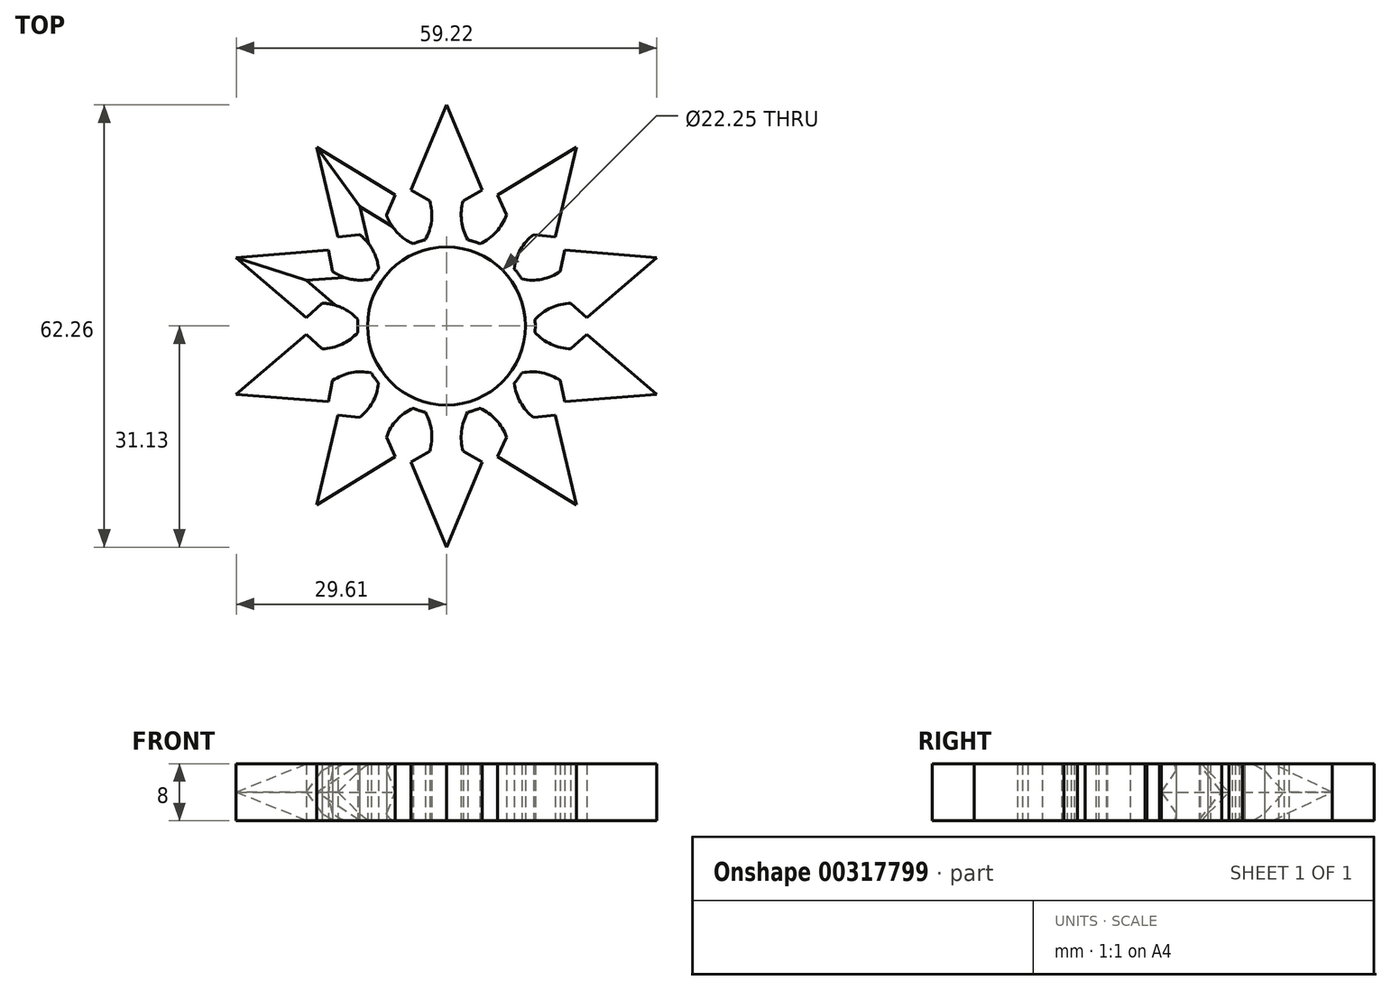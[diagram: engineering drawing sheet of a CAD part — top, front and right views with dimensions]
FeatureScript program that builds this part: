
annotation { "Feature Type Name" : "Feature", "Feature Type Description" : "" }
export const myFeature = defineFeature(function(context is Context, id is Id, definition is map)
    precondition{}
    {
        {
            var Q0;
            Q0=qCreatedBy(makeId("Top.planeOp"),FACE);
            var sketch = newSketch(context, id + "F0", { "sketchPlane" : qUnion([Q0])});
            skCircle(sketch, "E0", {"center": v(0, 0) * mm, "radius": 12.5 * mm});
            skLineSegment(sketch, "E1", {"start": v(0, 0) * mm, "end": v(0, 12.5) * mm, "construction": true});
            skPoint(sketch, "E2", {"position": v(3, 12.13) * mm});
            skPoint(sketch, "E3", {"position": v(-3, 12.13) * mm});
            skLineSegment(sketch, "E4", {"start": v(-3, 12.13) * mm, "end": v(-3, 19.13) * mm, "construction": true});
            skLineSegment(sketch, "E5", {"start": v(3, 12.13) * mm, "end": v(3, 19.13) * mm, "construction": true});
            skArc(sketch, "E6", {"start": v(-3, 12.13) * mm, "mid": v(-2.06, 15.63) * mm, "end": v(-3, 19.13) * mm});
            skArc(sketch, "E7", {"start": v(3, 19.13) * mm, "mid": v(2.06, 15.63) * mm, "end": v(3, 12.13) * mm});
            skLineSegment(sketch, "E8", {"start": v(-3, 19.13) * mm, "end": v(3, 19.13) * mm});
            skLineSegment(sketch, "E9", {"start": v(3, 19.13) * mm, "end": v(5, 19.13) * mm});
            skLineSegment(sketch, "E10", {"start": v(5, 19.13) * mm, "end": v(-3, 19.13) * mm});
            skLineSegment(sketch, "E11", {"start": v(-5, 19.13) * mm, "end": v(-3, 19.13) * mm});
            skLineSegment(sketch, "E12", {"start": v(0, 19.13) * mm, "end": v(0, 31.13) * mm, "construction": true});
            skLineSegment(sketch, "E13", {"start": v(-5, 19.13) * mm, "end": v(0, 31.13) * mm});
            skLineSegment(sketch, "E14", {"start": v(0, 31.13) * mm, "end": v(5, 19.13) * mm});
            skPoint(sketch, "E15", {"position": v(-2.35, 17.63) * mm});
            skPoint(sketch, "E16", {"position": v(2.35, 17.63) * mm});
            skLineSegment(sketch, "E17", {"start": v(-2.35, 17.63) * mm, "end": v(-5, 19.13) * mm});
            skLineSegment(sketch, "E18", {"start": v(2.35, 17.63) * mm, "end": v(5, 19.13) * mm});
            skArc(sketch, "E19.1.0", {"start": v(-9.56, 8.05) * mm, "mid": v(-10.86, 11.44) * mm, "end": v(-13.67, 13.72) * mm});
            skArc(sketch, "E19.1.1", {"start": v(-8.82, 17.24) * mm, "mid": v(-7.52, 13.86) * mm, "end": v(-4.7, 11.58) * mm});
            skLineSegment(sketch, "E19.1.2", {"start": v(-7.2, 18.42) * mm, "end": v(-13.67, 13.72) * mm});
            skLineSegment(sketch, "E19.1.3", {"start": v(-15.3, 12.54) * mm, "end": v(-13.67, 13.72) * mm});
            skLineSegment(sketch, "E19.1.4", {"start": v(-12.27, 12.88) * mm, "end": v(-15.3, 12.54) * mm});
            skLineSegment(sketch, "E19.1.5", {"start": v(-8.46, 15.65) * mm, "end": v(-7.2, 18.42) * mm});
            skLineSegment(sketch, "E19.1.6", {"start": v(-18.3, 25.19) * mm, "end": v(-7.2, 18.42) * mm});
            skLineSegment(sketch, "E19.1.7", {"start": v(-15.3, 12.54) * mm, "end": v(-18.3, 25.19) * mm});
            skArc(sketch, "E19.2.0", {"start": v(-12.47, 0.9) * mm, "mid": v(-15.5, 2.87) * mm, "end": v(-19.13, 3.06) * mm});
            skArc(sketch, "E19.2.1", {"start": v(-17.27, 8.77) * mm, "mid": v(-14.23, 6.8) * mm, "end": v(-10.61, 6.6) * mm});
            skLineSegment(sketch, "E19.2.2", {"start": v(-16.65, 10.67) * mm, "end": v(-19.13, 3.06) * mm});
            skLineSegment(sketch, "E19.2.3", {"start": v(-19.74, 1.16) * mm, "end": v(-19.13, 3.06) * mm});
            skLineSegment(sketch, "E19.2.4", {"start": v(-17.5, 3.21) * mm, "end": v(-19.74, 1.16) * mm});
            skLineSegment(sketch, "E19.2.5", {"start": v(-16.04, 7.69) * mm, "end": v(-16.65, 10.67) * mm});
            skLineSegment(sketch, "E19.2.6", {"start": v(-29.61, 9.62) * mm, "end": v(-16.65, 10.67) * mm});
            skLineSegment(sketch, "E19.2.7", {"start": v(-19.74, 1.16) * mm, "end": v(-29.61, 9.62) * mm});
            skArc(sketch, "E19.3.0", {"start": v(-10.61, -6.6) * mm, "mid": v(-14.23, -6.8) * mm, "end": v(-17.27, -8.77) * mm});
            skArc(sketch, "E19.3.1", {"start": v(-19.13, -3.06) * mm, "mid": v(-15.5, -2.87) * mm, "end": v(-12.47, -0.9) * mm});
            skLineSegment(sketch, "E19.3.2", {"start": v(-19.74, -1.16) * mm, "end": v(-17.27, -8.77) * mm});
            skLineSegment(sketch, "E19.3.3", {"start": v(-16.65, -10.67) * mm, "end": v(-17.27, -8.77) * mm});
            skLineSegment(sketch, "E19.3.4", {"start": v(-16.04, -7.69) * mm, "end": v(-16.65, -10.67) * mm});
            skLineSegment(sketch, "E19.3.5", {"start": v(-17.5, -3.21) * mm, "end": v(-19.74, -1.16) * mm});
            skLineSegment(sketch, "E19.3.6", {"start": v(-29.61, -9.62) * mm, "end": v(-19.74, -1.16) * mm});
            skLineSegment(sketch, "E19.3.7", {"start": v(-16.65, -10.67) * mm, "end": v(-29.61, -9.62) * mm});
            skArc(sketch, "E19.4.0", {"start": v(-4.7, -11.58) * mm, "mid": v(-7.52, -13.86) * mm, "end": v(-8.82, -17.24) * mm});
            skArc(sketch, "E19.4.1", {"start": v(-13.67, -13.72) * mm, "mid": v(-10.86, -11.44) * mm, "end": v(-9.56, -8.05) * mm});
            skLineSegment(sketch, "E19.4.2", {"start": v(-15.3, -12.54) * mm, "end": v(-8.82, -17.24) * mm});
            skLineSegment(sketch, "E19.4.3", {"start": v(-7.2, -18.42) * mm, "end": v(-8.82, -17.24) * mm});
            skLineSegment(sketch, "E19.4.4", {"start": v(-8.46, -15.65) * mm, "end": v(-7.2, -18.42) * mm});
            skLineSegment(sketch, "E19.4.5", {"start": v(-12.27, -12.88) * mm, "end": v(-15.3, -12.54) * mm});
            skLineSegment(sketch, "E19.4.6", {"start": v(-18.3, -25.19) * mm, "end": v(-15.3, -12.54) * mm});
            skLineSegment(sketch, "E19.4.7", {"start": v(-7.2, -18.42) * mm, "end": v(-18.3, -25.19) * mm});
            skArc(sketch, "E19.5.0", {"start": v(3, -12.13) * mm, "mid": v(2.06, -15.63) * mm, "end": v(3, -19.13) * mm});
            skArc(sketch, "E19.5.1", {"start": v(-3, -19.13) * mm, "mid": v(-2.06, -15.63) * mm, "end": v(-3, -12.13) * mm});
            skLineSegment(sketch, "E19.5.2", {"start": v(-5, -19.13) * mm, "end": v(3, -19.13) * mm});
            skLineSegment(sketch, "E19.5.3", {"start": v(5, -19.13) * mm, "end": v(3, -19.13) * mm});
            skLineSegment(sketch, "E19.5.4", {"start": v(2.35, -17.63) * mm, "end": v(5, -19.13) * mm});
            skLineSegment(sketch, "E19.5.5", {"start": v(-2.35, -17.63) * mm, "end": v(-5, -19.13) * mm});
            skLineSegment(sketch, "E19.5.6", {"start": v(0, -31.13) * mm, "end": v(-5, -19.13) * mm});
            skLineSegment(sketch, "E19.5.7", {"start": v(5, -19.13) * mm, "end": v(0, -31.13) * mm});
            skArc(sketch, "E19.6.0", {"start": v(9.56, -8.05) * mm, "mid": v(10.86, -11.44) * mm, "end": v(13.67, -13.72) * mm});
            skArc(sketch, "E19.6.1", {"start": v(8.82, -17.24) * mm, "mid": v(7.52, -13.86) * mm, "end": v(4.7, -11.58) * mm});
            skLineSegment(sketch, "E19.6.2", {"start": v(7.2, -18.42) * mm, "end": v(13.67, -13.72) * mm});
            skLineSegment(sketch, "E19.6.3", {"start": v(15.3, -12.54) * mm, "end": v(13.67, -13.72) * mm});
            skLineSegment(sketch, "E19.6.4", {"start": v(12.27, -12.88) * mm, "end": v(15.3, -12.54) * mm});
            skLineSegment(sketch, "E19.6.5", {"start": v(8.46, -15.65) * mm, "end": v(7.2, -18.42) * mm});
            skLineSegment(sketch, "E19.6.6", {"start": v(18.3, -25.19) * mm, "end": v(7.2, -18.42) * mm});
            skLineSegment(sketch, "E19.6.7", {"start": v(15.3, -12.54) * mm, "end": v(18.3, -25.19) * mm});
            skArc(sketch, "E19.7.0", {"start": v(12.47, -0.9) * mm, "mid": v(15.5, -2.87) * mm, "end": v(19.13, -3.06) * mm});
            skArc(sketch, "E19.7.1", {"start": v(17.27, -8.77) * mm, "mid": v(14.23, -6.8) * mm, "end": v(10.61, -6.6) * mm});
            skLineSegment(sketch, "E19.7.2", {"start": v(16.65, -10.67) * mm, "end": v(19.13, -3.06) * mm});
            skLineSegment(sketch, "E19.7.3", {"start": v(19.74, -1.16) * mm, "end": v(19.13, -3.06) * mm});
            skLineSegment(sketch, "E19.7.4", {"start": v(17.5, -3.21) * mm, "end": v(19.74, -1.16) * mm});
            skLineSegment(sketch, "E19.7.5", {"start": v(16.04, -7.69) * mm, "end": v(16.65, -10.67) * mm});
            skLineSegment(sketch, "E19.7.6", {"start": v(29.61, -9.62) * mm, "end": v(16.65, -10.67) * mm});
            skLineSegment(sketch, "E19.7.7", {"start": v(19.74, -1.16) * mm, "end": v(29.61, -9.62) * mm});
            skArc(sketch, "E19.8.0", {"start": v(10.61, 6.6) * mm, "mid": v(14.23, 6.8) * mm, "end": v(17.27, 8.77) * mm});
            skArc(sketch, "E19.8.1", {"start": v(19.13, 3.06) * mm, "mid": v(15.5, 2.87) * mm, "end": v(12.47, 0.9) * mm});
            skLineSegment(sketch, "E19.8.2", {"start": v(19.74, 1.16) * mm, "end": v(17.27, 8.77) * mm});
            skLineSegment(sketch, "E19.8.3", {"start": v(16.65, 10.67) * mm, "end": v(17.27, 8.77) * mm});
            skLineSegment(sketch, "E19.8.4", {"start": v(16.04, 7.69) * mm, "end": v(16.65, 10.67) * mm});
            skLineSegment(sketch, "E19.8.5", {"start": v(17.5, 3.21) * mm, "end": v(19.74, 1.16) * mm});
            skLineSegment(sketch, "E19.8.6", {"start": v(29.61, 9.62) * mm, "end": v(19.74, 1.16) * mm});
            skLineSegment(sketch, "E19.8.7", {"start": v(16.65, 10.67) * mm, "end": v(29.61, 9.62) * mm});
            skArc(sketch, "E19.9.0", {"start": v(4.7, 11.58) * mm, "mid": v(7.52, 13.86) * mm, "end": v(8.82, 17.24) * mm});
            skArc(sketch, "E19.9.1", {"start": v(13.67, 13.72) * mm, "mid": v(10.86, 11.44) * mm, "end": v(9.56, 8.05) * mm});
            skLineSegment(sketch, "E19.9.2", {"start": v(15.3, 12.54) * mm, "end": v(8.82, 17.24) * mm});
            skLineSegment(sketch, "E19.9.3", {"start": v(7.2, 18.42) * mm, "end": v(8.82, 17.24) * mm});
            skLineSegment(sketch, "E19.9.4", {"start": v(8.46, 15.65) * mm, "end": v(7.2, 18.42) * mm});
            skLineSegment(sketch, "E19.9.5", {"start": v(12.27, 12.88) * mm, "end": v(15.3, 12.54) * mm});
            skLineSegment(sketch, "E19.9.6", {"start": v(18.3, 25.19) * mm, "end": v(15.3, 12.54) * mm});
            skLineSegment(sketch, "E19.9.7", {"start": v(7.2, 18.42) * mm, "end": v(18.3, 25.19) * mm});
            skCircle(sketch, "E20", {"center": v(0, 0) * mm, "radius": 11.12 * mm});
            skSolve(sketch);
        }
        {
            var Q0;
            Q0 = qSketchRegion(id + "F0", true);
            extrude(context, id + "F1", {"entities" : qUnion([Q0]), "depth" : 8 * mm});
        }
        {
            var Q0;
            Q0=makeQuery(id+"F1.opExtrude","CAP_EDGE",EDGE,{"disambiguationData":[OSD([sQuery(id+"F0.wireOp",EDGE,"E19.1.7")])],"isStart":false});
            var Q1;
            Q1=makeQuery(id+"F1.opExtrude","CAP_EDGE",EDGE,{"disambiguationData":[OSD([sQuery(id+"F0.wireOp",EDGE,"E19.1.6")])],"isStart":false});
            var Q2;
            Q2=makeQuery(id+"F1.opExtrude","CAP_EDGE",EDGE,{"disambiguationData":[OSD([sQuery(id+"F0.wireOp",EDGE,"E19.1.6")])],"isStart":true});
            var Q3;
            Q3=makeQuery(id+"F1.opExtrude","CAP_EDGE",EDGE,{"disambiguationData":[OSD([sQuery(id+"F0.wireOp",EDGE,"E19.1.7")])],"isStart":true});
            var Q4;
            Q4=makeQuery(id+"F1.opExtrude","CAP_EDGE",EDGE,{"disambiguationData":[OSD([sQuery(id+"F0.wireOp",EDGE,"E19.2.6")])],"isStart":false});
            var Q5;
            Q5=makeQuery(id+"F1.opExtrude","CAP_EDGE",EDGE,{"disambiguationData":[OSD([sQuery(id+"F0.wireOp",EDGE,"E19.2.7")])],"isStart":false});
            var Q6;
            Q6=makeQuery(id+"F1.opExtrude","CAP_EDGE",EDGE,{"disambiguationData":[OSD([sQuery(id+"F0.wireOp",EDGE,"E19.2.7")])],"isStart":true});
            var Q7;
            Q7=makeQuery(id+"F1.opExtrude","CAP_EDGE",EDGE,{"disambiguationData":[OSD([sQuery(id+"F0.wireOp",EDGE,"E19.2.6")])],"isStart":true});
            chamfer(context, id + "F2", {"entities" : qUnion([Q0, Q1, Q2, Q3, Q4, Q5, Q6, Q7]), "width" : 4 * mm, "tangentPropagation" : true});
        }
    });
